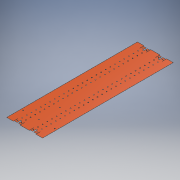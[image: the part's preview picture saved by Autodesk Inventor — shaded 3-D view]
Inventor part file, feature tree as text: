
AUTODESK INVENTOR PART (.ipt)
format: ipt  version: 2019 (Build 230136000, 136)  size: 425,472 bytes
history: native  units: mm
features: mirror x5, extrude x4, other x4
ambient origin geometry x8: Origin, YZ Plane, XZ Plane, XY Plane, X Axis, Y Axis, Z Axis, Center Point
bodies: Solid1 (feature_tree)
feature tree (13):
  extrude  "Skin Body"  Depth=1829.0mm
  extrude  "Feature Cut"  Depth=914.5mm
  mirror  "Feature Cut Side Mirror"
  mirror  "Feature Cut Mirror"
  extrude  "End Cut"  Depth=424.0mm
  mirror  "End Cut Mirror"
  extrude  "Slot Cut"  Depth=212.0mm
  mirror  "Slot Cut Side Mirror"
  mirror  "Slot Cut Mirror"
  other  "Skin Scheme"
  other  "Feature Cut Outline"
  other  "End Cut Outline"
  other  "Slot Cut Outline"
